# Revit family: FP_Revit_18_CE304DTB1_Cooktop_90000824A
name_source: partatom
category: Specialty Equipment
revit_build: Autodesk Revit 2018 (Build: 20170223_1515(x64)
units: mm (PartAtom-declared; Revit-internal decimal feet)

## family parameters
Always vertical = Yes
Cut with Voids When Loaded = Yes
OmniClass Number = 23.40.40.14.17.11
OmniClass Title = Cookers, Ovens, Stoves
Part Type = Normal
Room Calculation Point = No
Round Connector Dimension = Use Diameter
Shared = No
Work Plane-Based = No

## types (1)
- FP_Revit_18_CE304DTB1_Cooktop_90000824A
    Cavity - Depth = 495 mm  [stored 1.62402 ft]
    Cavity - Height = 110 mm  [stored 0.360892 ft]
    Cavity - Width = 700 mm  [stored 2.29659 ft]
    Chassis - Depth = 490 mm  [stored 1.60761 ft]
    Chassis - Height = 80 mm
    Chassis - Width = 689 mm  [stored 2.2605 ft]
    Clearance - Below = 115 mm  [stored 0.377297 ft]
    Clearance - Overhead Combustible = 762 mm  [stored 2.5 ft]
    Clearance - Overhead Non-Combustible = 610 mm  [stored 2.00131 ft]
    Clearance - Overhead Rangehood = 650 mm  [stored 2.13255 ft]
    Clearance - Rear Combustible = 55 mm  [stored 0.180446 ft]
    Clearance - Side Combustible = 55 mm  [stored 0.180446 ft]
    Connector Note - Electrical = 208 or 240 V, 60 Hz, 23 A or 26 A
    Description = 30" Electric Cooktop
    Manufacturer = Fisher & Paykel Appliances
    Material - Body = Fisher & Paykel - Grey
    Material - Cooktop = Fisher & Paykel - Glass, Black
    Material - Graphics = Fisher & Paykel - Graphics Grey
    Model = CE304DTB1
    Product - Depth = 530 mm  [stored 1.73885 ft]
    Product - Height = 115 mm  [stored 0.377297 ft]
    Product - Width = 750 mm  [stored 2.46063 ft]
    URL = www.fisherpaykel.com
    Visibility - Clearance Required = Yes

note: [stored X ft] marks values corroborated as IEEE doubles in the binary element streams (Revit-internal decimal feet)

## geometry (parser evidence)
native form markers: Sweep x8
no freeform markers — native parametric forms only
